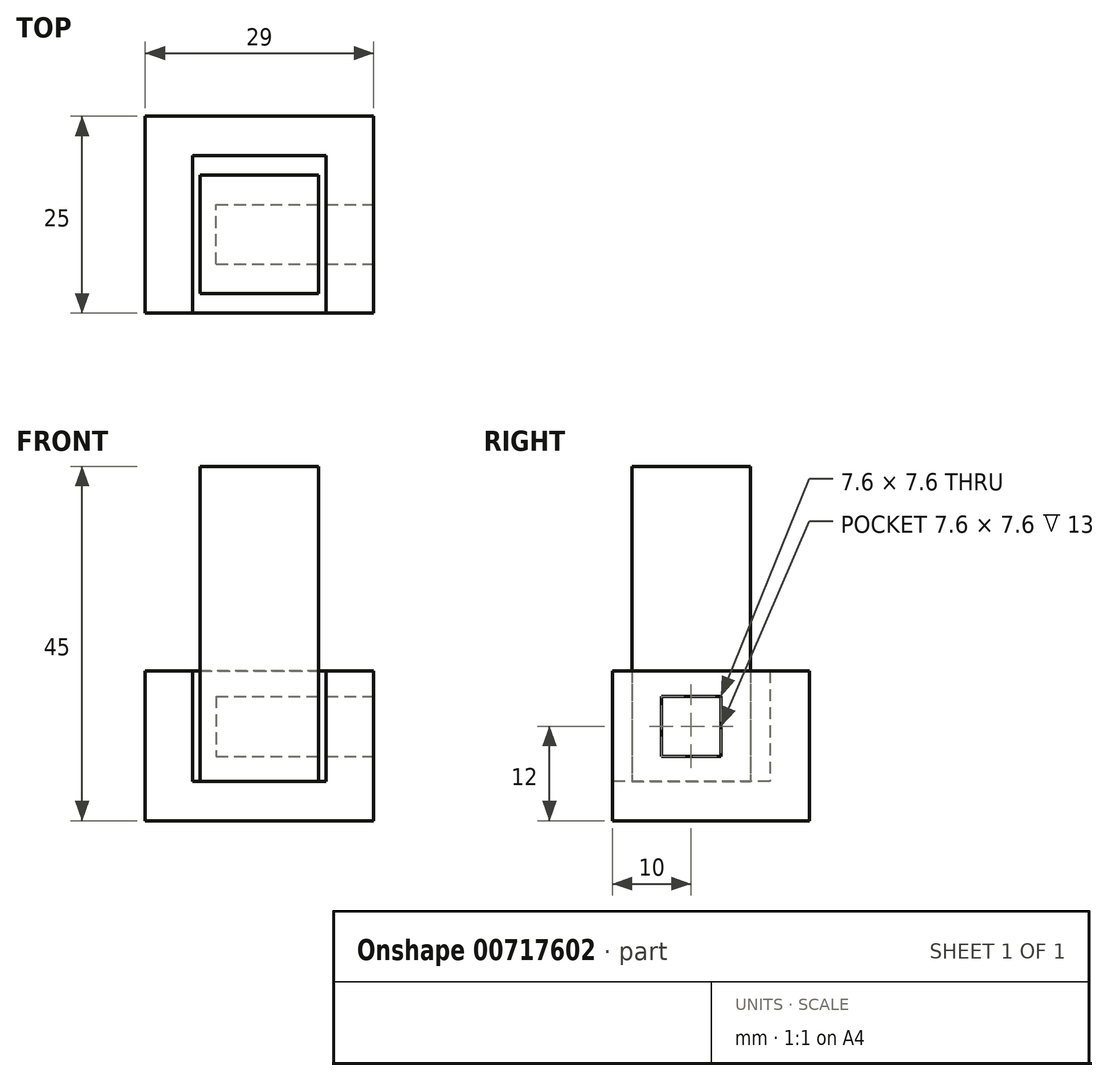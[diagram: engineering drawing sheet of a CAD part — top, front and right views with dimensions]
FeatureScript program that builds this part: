
annotation { "Feature Type Name" : "Feature", "Feature Type Description" : "" }
export const myFeature = defineFeature(function(context is Context, id is Id, definition is map)
    precondition{}
    {
        {
            var Q0;
            Q0=qCreatedBy(makeId("Top.planeOp"),FACE);
            var sketch = newSketch(context, id + "F0", { "sketchPlane" : qUnion([Q0])});
            skLineSegment(sketch, "E0.bottom", {"start": v(0, 2.5) * mm, "end": v(15, 2.5) * mm});
            skLineSegment(sketch, "E0.top", {"start": v(0, 17.5) * mm, "end": v(15, 17.5) * mm});
            skLineSegment(sketch, "E0.left", {"start": v(0, 2.5) * mm, "end": v(0, 17.5) * mm});
            skLineSegment(sketch, "E0.right", {"start": v(15, 2.5) * mm, "end": v(15, 17.5) * mm});
            skSolve(sketch);
        }
        {
            var Q0;
            Q0=makeQuery(id+"F0.imprint","IMPRINT",FACE,{"disambiguationData":[TD([[makeQuery(id+"F0.imprint","IMPRINT",EDGE,{"derivedFrom":sQuery(id+"F0.wireOp",EDGE,"E0.bottom")}),1.0]])]});
            extrude(context, id + "F1", {"entities" : qUnion([Q0]), "depth" : 40 * mm, "offsetDistance" : 25 * mm});
        }
        {
            var Q0;
            Q0=qCreatedBy(makeId("Top.planeOp"),FACE);
            var sketch = newSketch(context, id + "F2", { "sketchPlane" : qUnion([Q0])});
            skLineSegment(sketch, "E1", {"start": v(-1, 0) * mm, "end": v(-1, 20) * mm});
            skLineSegment(sketch, "E2", {"start": v(-1, 20) * mm, "end": v(16, 20) * mm});
            skLineSegment(sketch, "E3", {"start": v(16, 20) * mm, "end": v(16, 0) * mm});
            skLineSegment(sketch, "E4", {"start": v(16, 0) * mm, "end": v(22, 0) * mm});
            skLineSegment(sketch, "E5", {"start": v(22, 0) * mm, "end": v(22, 25) * mm});
            skLineSegment(sketch, "E6", {"start": v(22, 25) * mm, "end": v(-7, 25) * mm});
            skLineSegment(sketch, "E7", {"start": v(-7, 25) * mm, "end": v(-7, 0) * mm});
            skLineSegment(sketch, "E8", {"start": v(-7, 0) * mm, "end": v(-1, 0) * mm});
            skLineSegment(sketch, "E9", {"start": v(-1, 0) * mm, "end": v(16, 0) * mm});
            skSolve(sketch);
        }
        {
            var Q0;
            Q0=makeQuery(id+"F2.imprint","IMPRINT",FACE,{"disambiguationData":[TD([[makeQuery(id+"F2.imprint","IMPRINT",EDGE,{"derivedFrom":sQuery(id+"F2.wireOp",EDGE,"E1")}),1.0]])]});
            extrude(context, id + "F3", {"entities" : qUnion([Q0]), "depth" : 14 * mm, "offsetDistance" : 25 * mm});
        }
        {
            var Q0;
            Q0=makeQuery(id+"F3.opExtrude","SWEPT_FACE",FACE,{"disambiguationData":[OSD([sQuery(id+"F2.wireOp",EDGE,"E5")])]});
            cPlane(context, id + "F4", {"entities" : qUnion([Q0]), "cplaneType" : CPlaneType.OFFSET, "offset" : 0 * mm, "width" : 150 * mm, "height" : 150 * mm});
        }
        {
            var Q0;
            Q0=qCreatedBy(id+"F4.planeOp",FACE);
            var sketch = newSketch(context, id + "F5", { "sketchPlane" : qUnion([Q0])});
            skLineSegment(sketch, "E10.bottom", {"start": v(6.2, 10.8) * mm, "end": v(13.8, 10.8) * mm});
            skLineSegment(sketch, "E10.top", {"start": v(6.2, 3.2) * mm, "end": v(13.8, 3.2) * mm});
            skLineSegment(sketch, "E10.left", {"start": v(6.2, 10.8) * mm, "end": v(6.2, 3.2) * mm});
            skLineSegment(sketch, "E10.right", {"start": v(13.8, 10.8) * mm, "end": v(13.8, 3.2) * mm});
            skSolve(sketch);
        }
        {
            var Q0;
            Q0=makeQuery(id+"F5.imprint","IMPRINT",FACE,{"disambiguationData":[TD([[makeQuery(id+"F5.imprint","IMPRINT",EDGE,{"derivedFrom":sQuery(id+"F5.wireOp",EDGE,"E10.bottom")}),-1.0]])]});
            extrude(context, id + "F6", {"entities" : qUnion([Q0]), "operationType" : NewBodyOperationType.REMOVE, "oppositeDirection" : true, "depth" : 20 * mm, "offsetDistance" : 25 * mm});
        }
        {
            var Q0;
            Q0=makeQuery(id+"F2.imprint","IMPRINT",FACE,{"disambiguationData":[TD([[makeQuery(id+"F2.imprint","IMPRINT",EDGE,{"derivedFrom":sQuery(id+"F2.wireOp",EDGE,"E1")}),1.0]])]});
            var Q1;
            Q1=makeQuery(id+"F2.imprint","IMPRINT",FACE,{"disambiguationData":[TD([[makeQuery(id+"F2.imprint","IMPRINT",EDGE,{"derivedFrom":sQuery(id+"F2.wireOp",EDGE,"E1")}),-1.0]])]});
            extrude(context, id + "F7", {"entities" : qUnion([Q0, Q1]), "operationType" : NewBodyOperationType.ADD, "oppositeDirection" : true, "depth" : 5 * mm, "offsetDistance" : 25 * mm});
        }
    });
